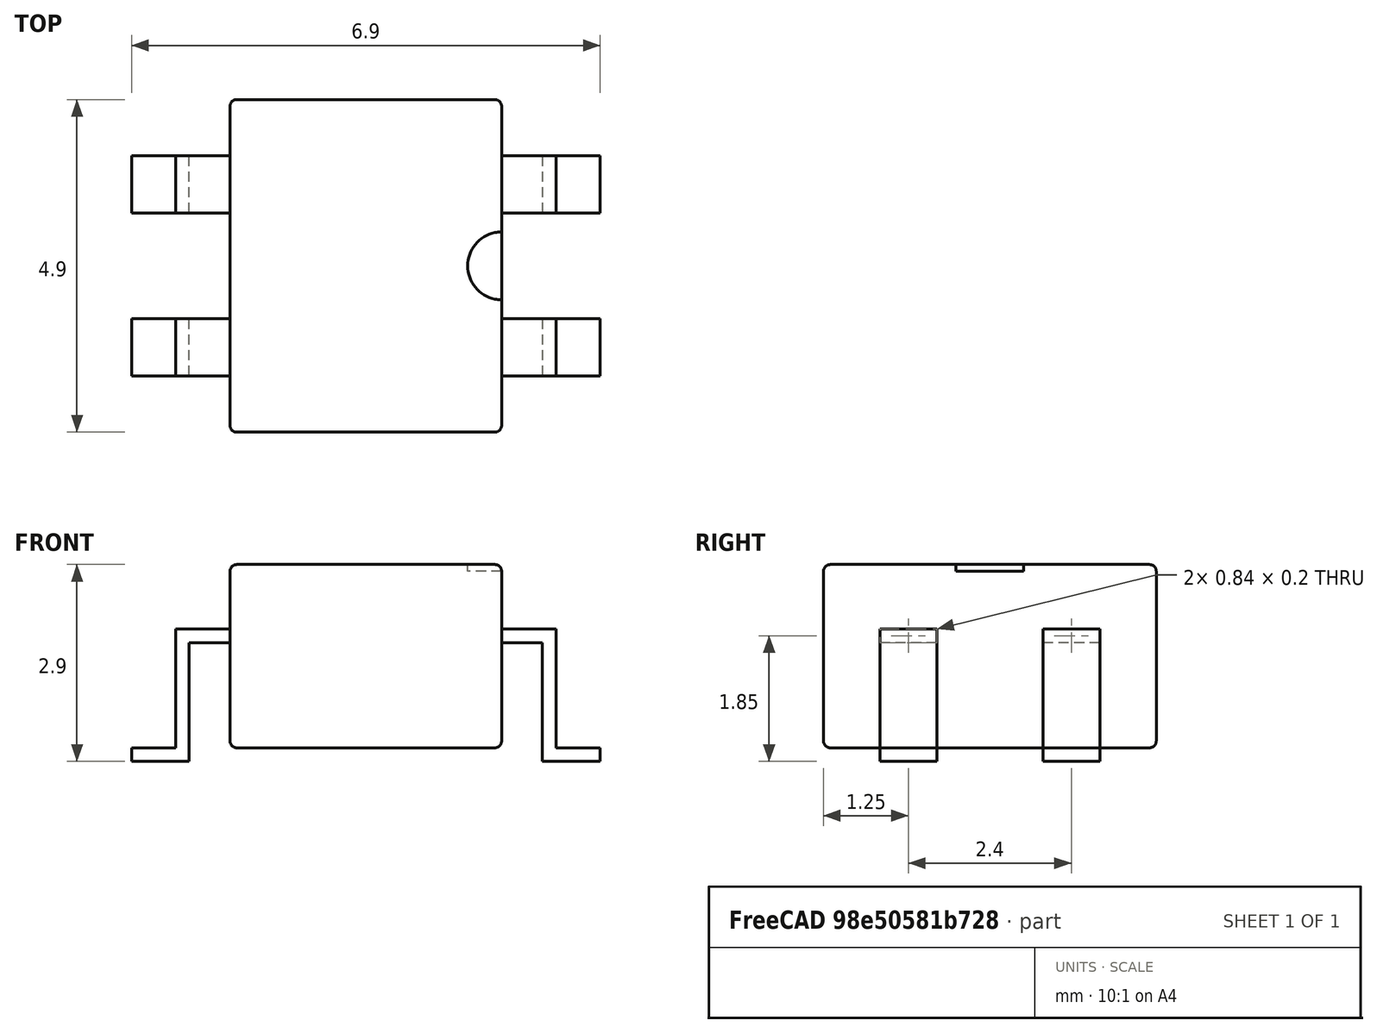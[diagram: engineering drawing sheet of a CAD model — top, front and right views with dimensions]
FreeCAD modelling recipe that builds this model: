
FCSTD DOCUMENT
Label: MBS_rectifier
objects: Part::Cut×5, Part::Box×4, Part::MultiFuse×3, Part::Cylinder×1, Part::Fillet×1
note: 14 computed .brp shape members not serialized (recipe doc carries the construction recipe); baked Part::Feature solids carry a one-line shape summary decoded from their .brp

FEATURE [Part::Cylinder] Cylinder
  Angle = 360
  Height = 1
  Placement = pos=(2,0,2.8) rot=(0,0,1;0rad)
  Radius = 0.5
FEATURE [Part::Box] Box
  Height = 2.7
  Length = 4
  Placement = pos=(-2,-2.45,0.2) rot=(0,0,1;0rad)
  Width = 4.9
FEATURE [Part::Fillet] Fillet
  Base = -> Box
  Edges = 12 edges r=0.1: [Edge1,Edge2,Edge3,Edge4,Edge5,Edge6,Edge7,Edge8,Edge9,Edge10,Edge11,Edge12]
FEATURE [Part::Cut] Cut  label="Grundkoerper"
  Base = -> Fillet
  Tool = -> Cylinder
FEATURE [Part::Box] Box001
  Height = 1.95
  Length = 1.45
  Width = 0.84
FEATURE [Part::Box] Box002
  Height = 1.75
  Length = 2
  Placement = pos=(0.85,0,0) rot=(0,0,1;0rad)
  Width = 2
FEATURE [Part::Box] Box003
  Height = 1.75
  Length = 2
  Placement = pos=(-1.35,0,0.2) rot=(0,0,1;0rad)
  Width = 2
FEATURE [Part::MultiFuse] Fusion
  Shapes = -> [Box002,Box003]
FEATURE [Part::Cut] Cut001  label="PIN"
  Base = -> Box001
  Placement = pos=(-3.45,0.78,0) rot=(0,0,1;0rad)
  Tool = -> Fusion
FEATURE [Part::Cut] Cut002  label="PIN001"
  Placement = pos=(-3.45,-1.62,0) rot=(0,0,1;0rad)
FEATURE [Part::Cut] Cut003  label="PIN002"
  Placement = pos=(3.45,-0.78,0) rot=(0,0,1;3.14159rad)
FEATURE [Part::Cut] Cut004  label="PIN003"
  Placement = pos=(3.45,1.62,0) rot=(0,0,1;3.14159rad)
FEATURE [Part::MultiFuse] Fusion001  label="Pins"
  Shapes = -> [Cut001,Cut002,Cut003,Cut004]
FEATURE [Part::MultiFuse] Fusion002  label="MBS"
  Shapes = -> [Cut,Fusion001]
